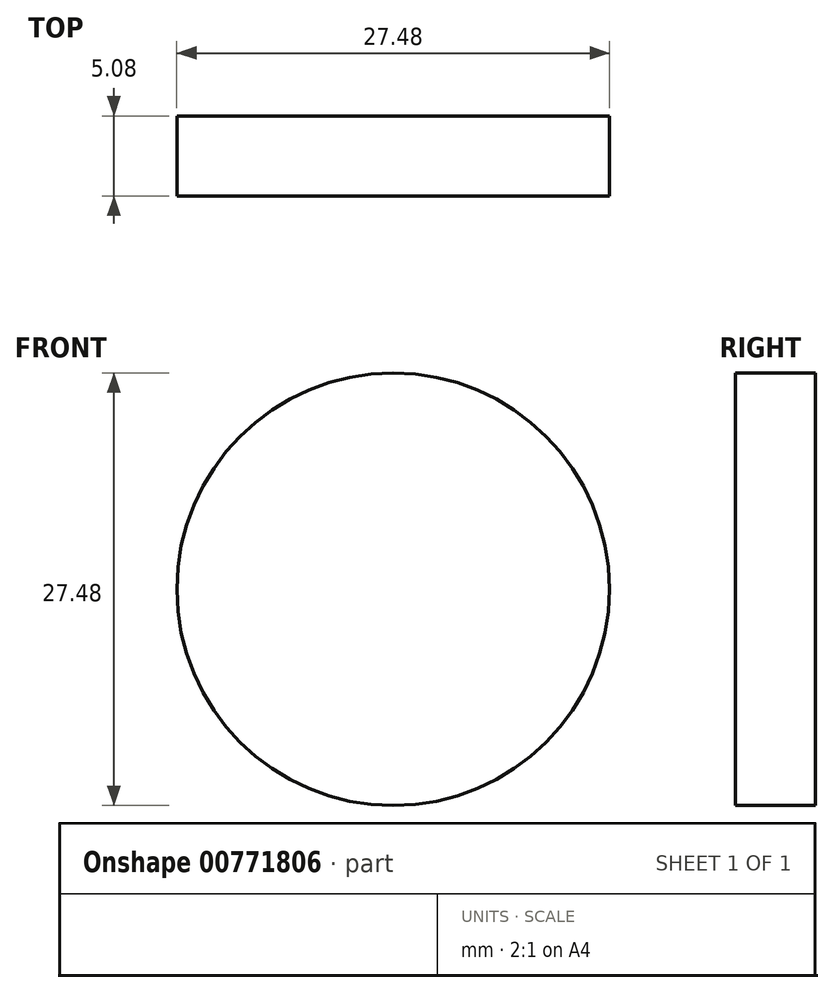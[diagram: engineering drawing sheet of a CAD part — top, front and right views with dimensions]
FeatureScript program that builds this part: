
annotation { "Feature Type Name" : "Feature", "Feature Type Description" : "" }
export const myFeature = defineFeature(function(context is Context, id is Id, definition is map)
    precondition{}
    {
        {
            var Q0;
            Q0=qCreatedBy(makeId("Front.planeOp"),FACE);
            var sketch = newSketch(context, id + "F0", { "sketchPlane" : qUnion([Q0])});
            skCircle(sketch, "E0", {"center": v(-16.13, 6.73) * mm, "radius": 13.74 * mm});
            skSolve(sketch);
        }
        {
            var Q0;
            Q0 = qSketchRegion(id + "F0", true);
            extrude(context, id + "F1", {"entities" : qUnion([Q0]), "depth" : 5.08 * mm, "offsetDistance" : 25.4 * mm});
        }
    });
